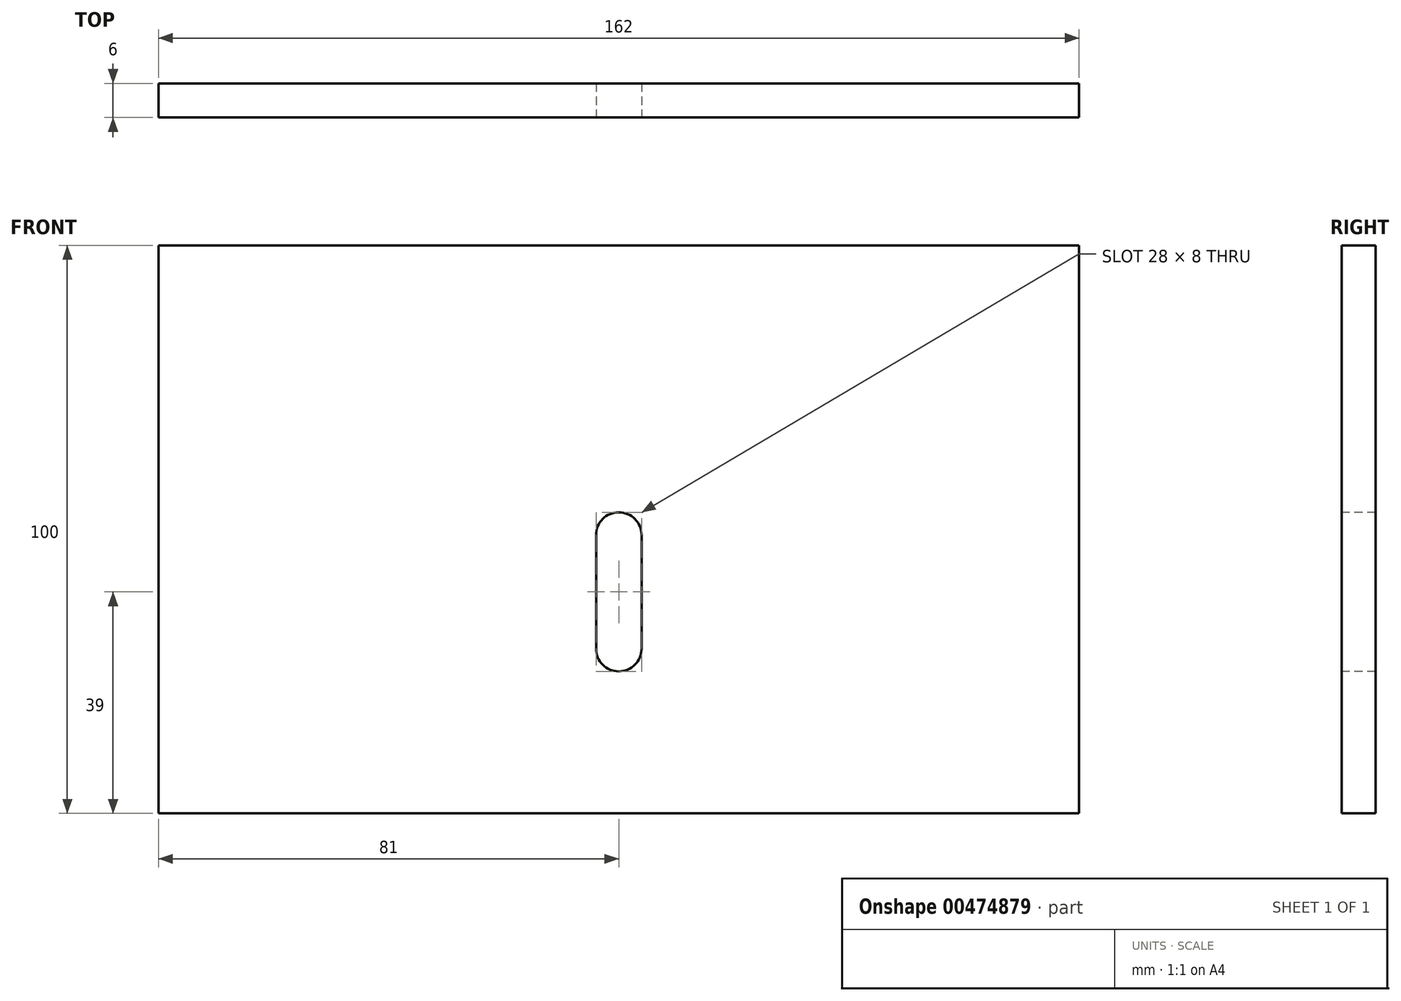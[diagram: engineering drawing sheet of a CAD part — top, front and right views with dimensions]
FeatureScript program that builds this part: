
annotation { "Feature Type Name" : "Feature", "Feature Type Description" : "" }
export const myFeature = defineFeature(function(context is Context, id is Id, definition is map)
    precondition{}
    {
        {
            var Q0;
            Q0=qCreatedBy(makeId("Front.planeOp"),FACE);
            var sketch = newSketch(context, id + "F0", { "sketchPlane" : qUnion([Q0])});
            skLineSegment(sketch, "E0.bottom", {"start": v(81, -50) * mm, "end": v(-81, -50) * mm});
            skLineSegment(sketch, "E0.top", {"start": v(81, 50) * mm, "end": v(-81, 50) * mm});
            skLineSegment(sketch, "E0.left", {"start": v(81, -50) * mm, "end": v(81, 50) * mm});
            skLineSegment(sketch, "E0.right", {"start": v(-81, -50) * mm, "end": v(-81, 50) * mm});
            skPoint(sketch, "E0.middle", {"position": v(0, 0) * mm});
            skSolve(sketch);
        }
        {
            var Q0;
            Q0=qSketchRegion(id+"F0",true);
            extrude(context, id + "F1", {"entities" : qUnion([Q0]), "endBound" : BoundingType.SYMMETRIC, "depth" : 6 * mm});
        }
        {
            var Q0;
            Q0=makeQuery(id+"F1.opExtrude","CAP_FACE",FACE,{"disambiguationData":[OSD([sQuery(id+"F0.wireOp",EDGE,"E0.bottom"),sQuery(id+"F0.wireOp",EDGE,"E0.top"),sQuery(id+"F0.wireOp",EDGE,"E0.left"),sQuery(id+"F0.wireOp",EDGE,"E0.right")])],"isStart":false});
            var sketch = newSketch(context, id + "F2", { "sketchPlane" : qUnion([Q0])});
            skLineSegment(sketch, "E1.left", {"start": v(4, -21) * mm, "end": v(4, -1) * mm});
            skLineSegment(sketch, "E1.right", {"start": v(-4, -21) * mm, "end": v(-4, -1) * mm});
            skPoint(sketch, "E1.middle", {"position": v(0, -11) * mm});
            skArc(sketch, "E2", {"start": v(-4, -21) * mm, "mid": v(0, -25) * mm, "end": v(4, -21) * mm});
            skArc(sketch, "E3", {"start": v(4, -1) * mm, "mid": v(0, 3) * mm, "end": v(-4, -1) * mm});
            skSolve(sketch);
        }
        {
            var Q0;
            Q0 = qSketchRegion(id + "F2", true);
            extrude(context, id + "F3", {"entities" : qUnion([Q0]), "operationType" : NewBodyOperationType.REMOVE, "oppositeDirection" : true, "depth" : 25 * mm});
        }
    });
